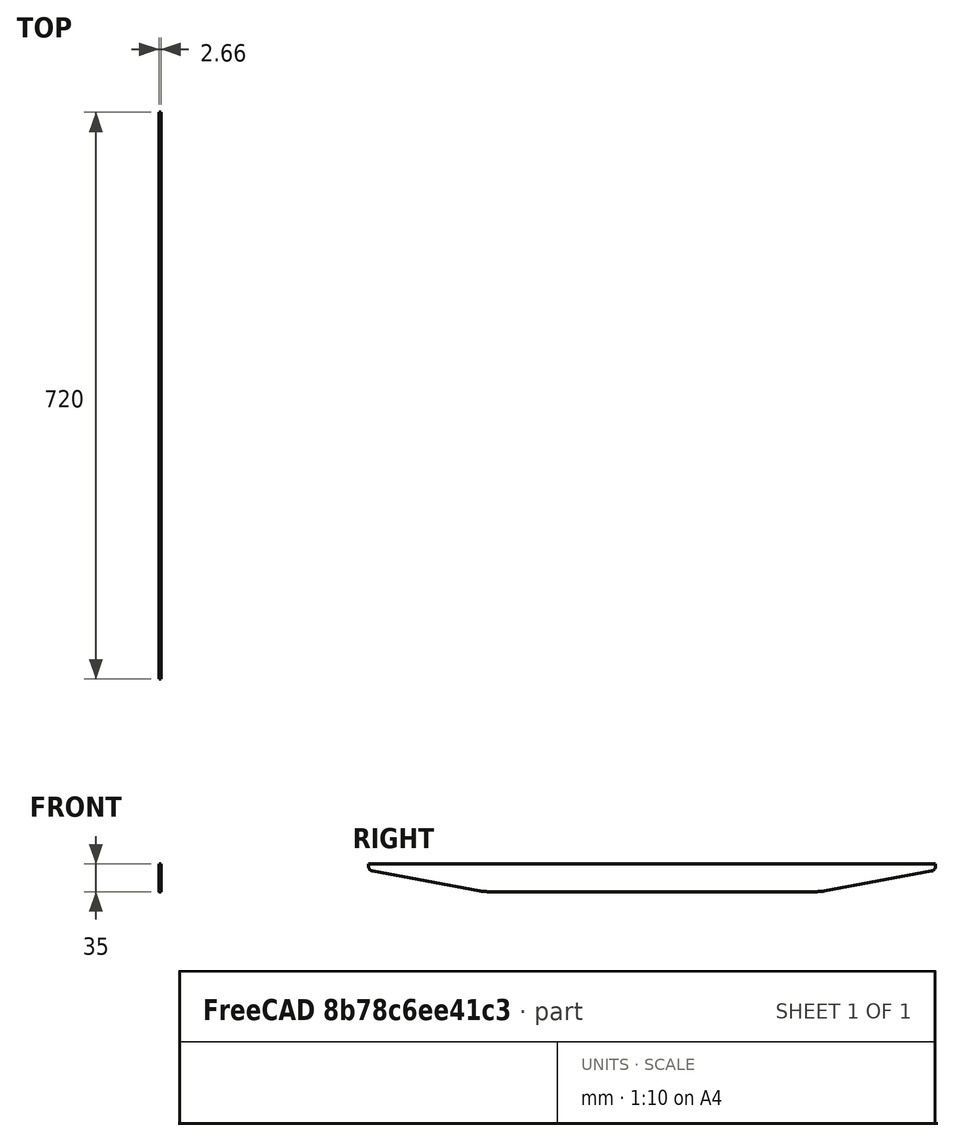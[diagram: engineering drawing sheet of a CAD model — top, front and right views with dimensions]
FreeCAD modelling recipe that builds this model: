
FCSTD DOCUMENT  (FreeCAD 0.20R29177 +426 (Git))
Label: ComputerPlatformRib
License: All rights reserved
LicenseURL: http://en.wikipedia.org/wiki/All_rights_reserved
objects: App::DocumentObjectGroup×3, PartDesign::CoordinateSystem×1, App::FeaturePython×1, Sketcher::SketchObject×1, PartDesign::Pad×1, PartDesign::Body×1, App::Part×1, TechDraw::DrawSVGTemplate×1, TechDraw::DrawViewPart×1, TechDraw::DrawPage×1
note: 5 computed .brp shape members not serialized (recipe doc carries the construction recipe); baked Part::Feature solids carry a one-line shape summary decoded from their .brp
EXTERNAL_REF file=Params.FCStd obj=Spreadsheet

FEATURE [App::DocumentObjectGroup] Parts
FEATURE [PartDesign::CoordinateSystem] LCS_Origin
  AttacherType = Attacher::AttachEngine3D
  MapMode = 2
  Support = -> [X_Axis]
FEATURE [App::FeaturePython] Variables  # WARN: FeaturePython — macro-defined, semantics opaque (R4)
  Type = App::PropertyContainer
FEATURE [App::DocumentObjectGroup] Constraints
FEATURE [App::DocumentObjectGroup] Configurations
FEATURE [Sketcher::SketchObject] Sketch
  FullyConstrained = true
  MapMode = 5
  Placement = pos=(0,0,0) rot=(0.57735,0.57735,0.57735;2.0944rad)
  Support = -> [YZ_Plane001]
  expr: Constraints[24] = <<Params>>#<<Params>>.FrontSkateOffset + 20
  sketch-geometry (12):
    g0: LineSegment StartX=-350 StartY=0 StartZ=0 EndX=370 EndY=0 EndZ=0
    g1: LineSegment StartX=370 StartY=0 StartZ=0 EndX=370 EndY=-3 EndZ=0
    g2: LineSegment StartX=-350 StartY=-3 StartZ=0 EndX=-350 EndY=0 EndZ=0
    g3: ArcOfCircle CenterX=-344 CenterY=-3 CenterZ=0 NormalX=0 NormalY=0 NormalZ=1 AngleXU=0 Radius=6 StartAngle=3.14159 EndAngle=4.5287
    g4: GeomPoint X=-350 Y=-7.98796 Z=0
    g5: ArcOfCircle CenterX=364 CenterY=-3 CenterZ=0 NormalX=0 NormalY=0 NormalZ=1 AngleXU=0 Radius=6 StartAngle=4.89608 EndAngle=6.28319
    g6: LineSegment StartX=365.096 StartY=-8.89906 StartZ=0 EndX=229.133 EndY=-34.1588 EndZ=0
    g7: LineSegment StartX=220 StartY=-35 StartZ=0 EndX=-200 EndY=-35 EndZ=0
    g8: LineSegment StartX=-209.133 StartY=-34.1588 StartZ=0 EndX=-345.096 EndY=-8.89906 EndZ=0
    g9: ArcOfCircle CenterX=-200 CenterY=15 CenterZ=0 NormalX=0 NormalY=0 NormalZ=1 AngleXU=0 Radius=50 StartAngle=4.5287 EndAngle=4.71239
    g10: GeomPoint X=-204.605 Y=-35 Z=0
    g11: ArcOfCircle CenterX=220 CenterY=15 CenterZ=0 NormalX=0 NormalY=0 NormalZ=1 AngleXU=0 Radius=50 StartAngle=4.71239 EndAngle=4.89608
  constraints (30):
    c: Coincident(g0,g1)
    c: Coincident(g2,g0)
    c: Horizontal(g0)
    c: Vertical(g1)
    c: Vertical(g2)
    c: PointOnObject(g0,g-1)
    c: PointOnObject(g4,g2)
    c: Tangent(g2,g3) = 1.5708
    c: Tangent(g8,g3) = 1.5708
    c: Tangent(g6,g5) = 1.5708
    c: Tangent(g1,g5) = 1.5708
    c: PointOnObject(g4,g8)
    c: Horizontal(g7)
    c: Radius(g3) = 6
    c: Radius(g5) = 6
    c: PointOnObject(g10,g8)
    c: PointOnObject(g10,g7)
    c: Tangent(g8,g9) = 1.5708
    c: Tangent(g7,g9) = 1.5708
    c: Tangent(g7,g11) = 1.5708
    c: Tangent(g6,g11) = 1.5708
    c: Equal(g11,g9)
    c: Radius(g9) = 50
    c: DistanceY(g7,g-1) = 35
    c: DistanceX(g-1,g0) = 370
    c: DistanceX(g0,g-1) = 350
    c: DistanceY(g2,g2) = 3
    c: Equal(g2,g1)
    c: DistanceX(g7,g0) = 150
    c: DistanceX(g0,g7) = 150
FEATURE [PartDesign::Pad] Pad
  Direction = (1,-2e-16,3e-16)
  Length = 2.656
  Length2 = 10
  Midplane = true
  Placement = pos=(0,0,0) rot=(0.57735,0.57735,0.57735;2.0944rad)
  Profile = -> Sketch
  ReferenceAxis = -> Sketch [N_Axis]
  Type = 0
  expr: Length = <<Params>>#<<Params>>.SheetMetalThickness
FEATURE [PartDesign::Body] Body
  Group = -> [Sketch,Pad]
  Origin = -> Origin001
  Tip = -> Pad
FEATURE [App::Part] Assembly
  AssemblyType = Part::Link
  Group = -> [LCS_Origin,Variables,Constraints,Configurations,Body]
  Origin = -> Origin
  Type = Assembly
FEATURE [TechDraw::DrawSVGTemplate] Template
  Height = 841
  Orientation = 1
  Width = 1189
FEATURE [TechDraw::DrawViewPart] View
  CoarseView = false
  Direction = (1,0,0)
  Focus = 100
  HardHidden = false
  IsoCount = 0
  IsoHidden = false
  IsoVisible = false
  LockPosition = false
  Perspective = false
  Rotation = 0
  ScaleType = 0
  SeamHidden = false
  SeamVisible = true
  SmoothHidden = false
  SmoothVisible = true
  Source = -> [Pad]
  X = 229.109
  XDirection = (0,0,-1)
  Y = 400.354
FEATURE [TechDraw::DrawPage] Page
  KeepUpdated = true
  NextBalloonIndex = 1
  ProjectionType = 0
  Template = -> Template
  Views = -> [View]
